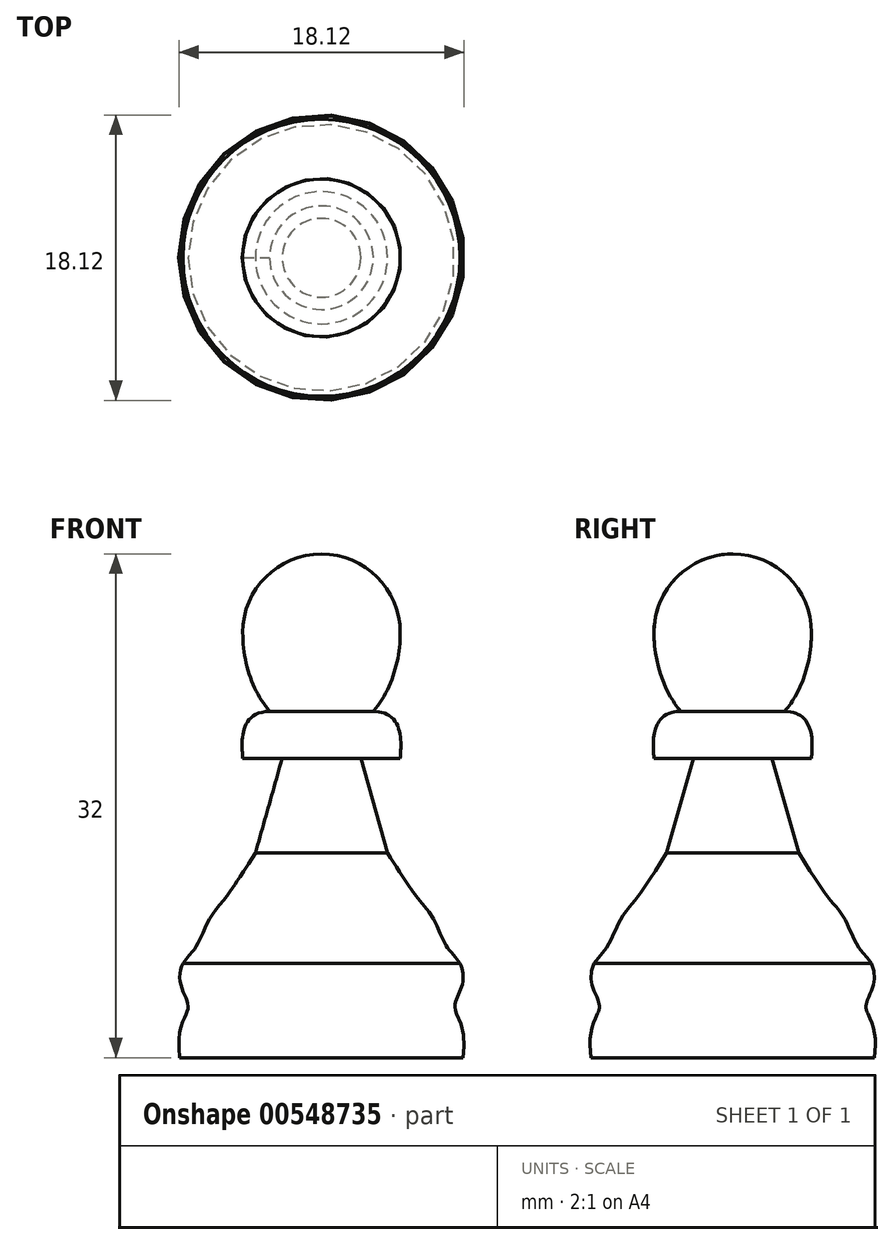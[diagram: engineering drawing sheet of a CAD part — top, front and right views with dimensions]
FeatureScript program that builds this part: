
annotation { "Feature Type Name" : "Feature", "Feature Type Description" : "" }
export const myFeature = defineFeature(function(context is Context, id is Id, definition is map)
    precondition{}
    {
        {
            var Q0;
            Q0=qCreatedBy(makeId("Right.planeOp"),FACE);
            var sketch = newSketch(context, id + "F0", { "sketchPlane" : qUnion([Q0])});
            skLineSegment(sketch, "E0", {"start": v(0, 0) * mm, "end": v(0, 32) * mm});
            skLineSegment(sketch, "E1", {"start": v(0, 0) * mm, "end": v(-9, 0) * mm});
            skPoint(sketch, "E2", {"position": v(0, 27) * mm});
            skArc(sketch, "E3", {"start": v(0, 32) * mm, "mid": v(-3.54, 30.54) * mm, "end": v(-5, 27) * mm});
            skLineSegment(sketch, "E4", {"start": v(0, 27) * mm, "end": v(-5, 27) * mm, "construction": true});
            skEllipticalArc(sketch, "E5", {});
            skPoint(sketch, "E6", {"position": v(0, 22) * mm});
            skPoint(sketch, "E7", {"position": v(0, 19) * mm});
            skLineSegment(sketch, "E8", {"start": v(-2.5, 19) * mm, "end": v(-5, 19) * mm});
            skPoint(sketch, "E9", {"position": v(0, 13) * mm});
            skPoint(sketch, "E10", {"position": v(-2.5, 19) * mm});
            skLineSegment(sketch, "E11", {"start": v(0, 13) * mm, "end": v(-4.2, 13) * mm, "construction": true});
            skLineSegment(sketch, "E12", {"start": v(-2.5, 19) * mm, "end": v(-4.2, 13) * mm});
            skPoint(sketch, "E13", {"position": v(0, 6) * mm});
            skPoint(sketch, "E14", {"position": v(0, 3) * mm});
            skLineSegment(sketch, "E15", {"start": v(0, 3) * mm, "end": v(-8.5, 3) * mm, "construction": true});
            skLineSegment(sketch, "E16", {"start": v(0, 6) * mm, "end": v(-8.8, 6) * mm, "construction": true});
            skPoint(sketch, "E17", {"position": v(0, 11) * mm});
            skPoint(sketch, "E18", {"position": v(0, 9) * mm});
            skPoint(sketch, "E19", {"position": v(0, 7) * mm});
            skLineSegment(sketch, "E20", {"start": v(0, 11) * mm, "end": v(-5.5, 11) * mm, "construction": true});
            skLineSegment(sketch, "E21", {"start": v(0, 9) * mm, "end": v(-7, 9) * mm, "construction": true});
            skLineSegment(sketch, "E22", {"start": v(0, 7) * mm, "end": v(-8, 7) * mm, "construction": true});
            skFitSpline(sketch, "E23", {"points": [v(-4.2, 13) * mm, v(-5.5, 11) * mm, v(-6.06, 10.2) * mm, v(-7, 9) * mm, v(-7.51, 7.95) * mm, v(-8, 7) * mm, v(-8.8, 6) * mm], "startDerivative": vector(-11.69, -18.6) * mm, "endDerivative": vector(-11.32, -14.93) * mm});
            skFitSpline(sketch, "E24", {"points": [v(-8.8, 6) * mm, v(-8.96, 4.77) * mm, v(-8.57, 3.7) * mm, v(-8.5, 3) * mm, v(-9, 0) * mm], "startDerivative": vector(-2.53, -4.34) * mm, "endDerivative": vector(2.15, -15.73) * mm});
            skFitSpline(sketch, "E25", {"points": [v(-5, 19) * mm, v(-3.3, 22) * mm], "startDerivative": vector(-0.12, 2.37) * mm, "endDerivative": vector(6.25, 0.14) * mm});
            const initialGuessF0  = {"E5": [0, 0.027, 0, -1, 0.0066423055231571194, 0.005, 4.71238898038469, 5.564619560337421]};
            skSetInitialGuess(sketch, initialGuessF0);
            skSolve(sketch);
        }
        {
            var Q0;
            Q0 = qSketchRegion(id + "F0", true);
            var Q1;
            Q1=sQuery(id+"F0.wireOp",EDGE,"E0");
            revolve(context, id + "F1", {"entities" : qUnion([Q0]), "axis" : qUnion([Q1]), "revolveType" : RevolveType.FULL});
        }
    });
